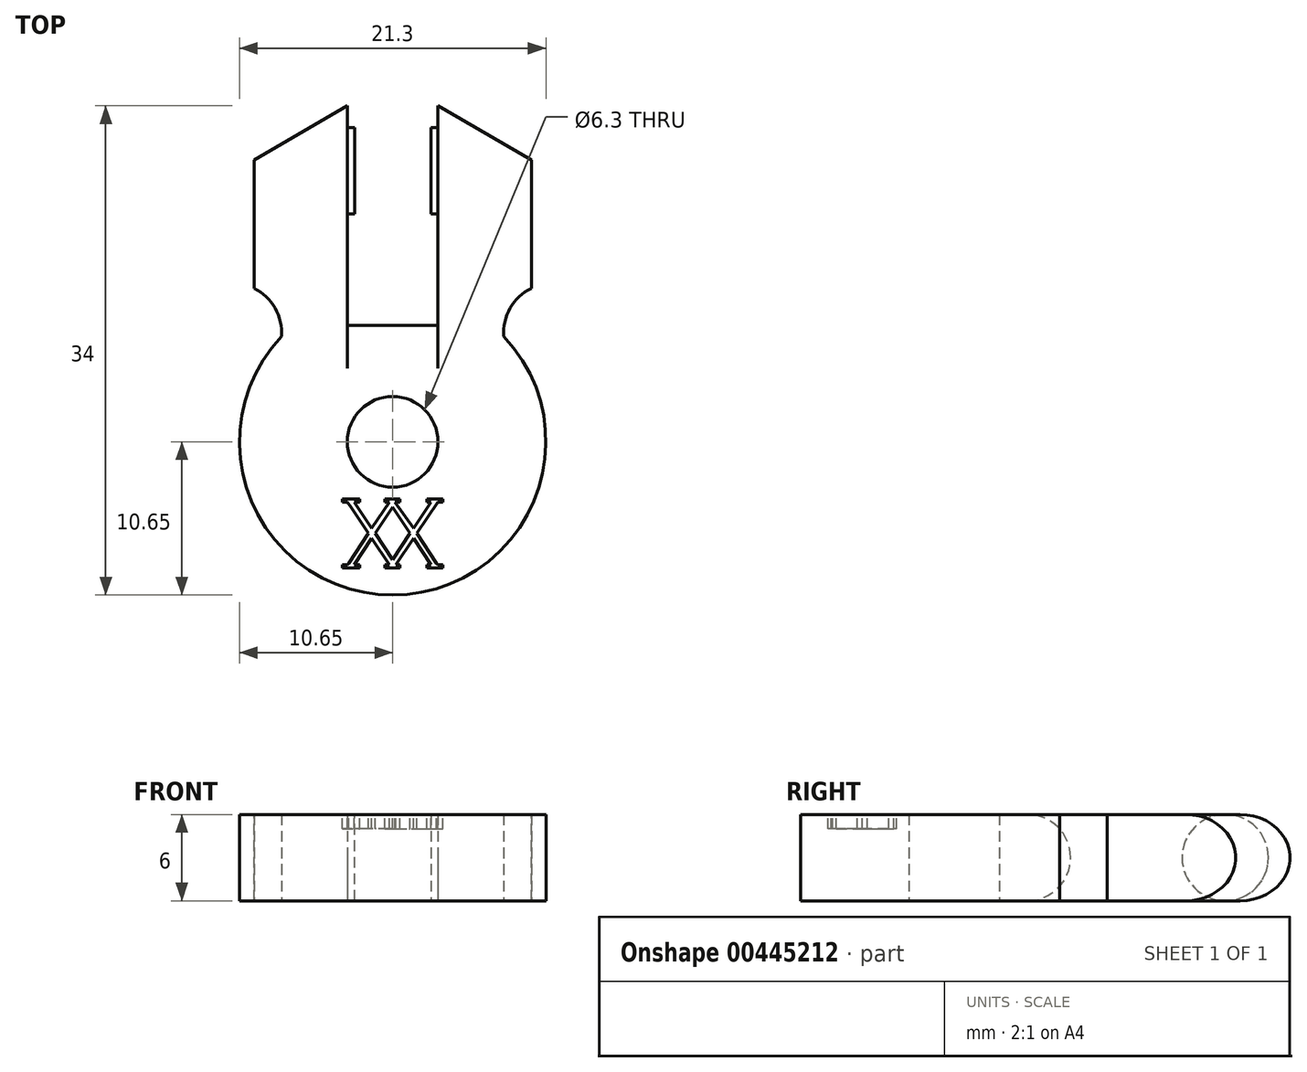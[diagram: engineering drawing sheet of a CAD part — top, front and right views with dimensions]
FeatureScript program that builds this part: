
annotation { "Feature Type Name" : "Feature", "Feature Type Description" : "" }
export const myFeature = defineFeature(function(context is Context, id is Id, definition is map)
    precondition{}
    {
        {
            var Q0;
            Q0=qCreatedBy(makeId("Top.planeOp"),FACE);
            var sketch = newSketch(context, id + "F0", { "sketchPlane" : qUnion([Q0])});
            skArc(sketch, "E0", {"start": v(-3.15, 10.17) * mm, "mid": v(0, -10.65) * mm, "end": v(3.15, 10.17) * mm});
            skCircle(sketch, "E1", {"center": v(0, 0) * mm, "radius": 3.15 * mm});
            skPoint(sketch, "E2", {"position": v(0, 8.1) * mm});
            skLineSegment(sketch, "E3", {"start": v(0, 8.1) * mm, "end": v(3.15, 8.1) * mm});
            skLineSegment(sketch, "E4", {"start": v(0, 8.1) * mm, "end": v(-3.15, 8.1) * mm});
            skLineSegment(sketch, "E5", {"start": v(0, 0) * mm, "end": v(0, 8.1) * mm});
            skLineSegment(sketch, "E6", {"start": v(-3.15, 8.1) * mm, "end": v(-3.15, 23.35) * mm});
            skLineSegment(sketch, "E7", {"start": v(-9.64, 19.59) * mm, "end": v(-9.64, 10.66) * mm});
            skLineSegment(sketch, "E8", {"start": v(-9.64, 19.59) * mm, "end": v(-3.15, 23.35) * mm});
            skArc(sketch, "E9", {"start": v(-7.72, 7.33) * mm, "mid": v(-8.17, 9.3) * mm, "end": v(-9.64, 10.66) * mm});
            skPoint(sketch, "E10.orphan", {"position": v(-9.64, 4.53) * mm});
            skLineSegment(sketch, "E11.MirrorCS", {"start": v(3.15, 8.1) * mm, "end": v(3.15, 23.35) * mm});
            skLineSegment(sketch, "E12.MirrorCS", {"start": v(9.64, 19.59) * mm, "end": v(3.15, 23.35) * mm});
            skLineSegment(sketch, "E13.MirrorCS", {"start": v(9.64, 19.59) * mm, "end": v(9.64, 10.66) * mm});
            skArc(sketch, "E14.MirrorCS", {"start": v(7.72, 7.33) * mm, "mid": v(8.17, 9.3) * mm, "end": v(9.64, 10.66) * mm});
            skSolve(sketch);
        }
        {
            var Q0;
            Q0=qSketchRegion(id+"F0",true);
            extrude(context, id + "F1", {"entities" : qUnion([Q0]), "depth" : 6 * mm});
        }
        {
            var Q0;
            Q0=makeQuery(id+"F1.opExtrude","SWEPT_FACE",FACE,{"disambiguationData":[OSD([sQuery(id+"F0.wireOp",EDGE,"E6")])]});
            var sketch = newSketch(context, id + "F2", { "sketchPlane" : qUnion([Q0])});
            skLineSegment(sketch, "E15", {"start": v(23.35, 6) * mm, "end": v(23.35, 0) * mm});
            skPoint(sketch, "E16", {"position": v(23.35, 3) * mm});
            skCircle(sketch, "E17", {"center": v(18.85, 3) * mm, "radius": 3 * mm});
            skSolve(sketch);
        }
        {
            var Q0;
            Q0=qSketchRegion(id+"F2",true);
            extrude(context, id + "F3", {"entities" : qUnion([Q0]), "operationType" : NewBodyOperationType.ADD, "depth" : 0.5 * mm});
        }
        {
            var Q0;
            Q0=makeQuery(id+"F1.opExtrude","SWEPT_FACE",FACE,{"disambiguationData":[OSD([sQuery(id+"F0.wireOp",EDGE,"E11.MirrorCS")])]});
            var sketch = newSketch(context, id + "F4", { "sketchPlane" : qUnion([Q0])});
            skPoint(sketch, "E18", {"position": v(-23.35, 3) * mm});
            skCircle(sketch, "E19", {"center": v(-18.85, 3) * mm, "radius": 3 * mm});
            skSolve(sketch);
        }
        {
            var Q0;
            Q0=qSketchRegion(id+"F4",true);
            extrude(context, id + "F5", {"entities" : qUnion([Q0]), "operationType" : NewBodyOperationType.ADD, "depth" : 0.5 * mm});
        }
        {
            var Q0;
            Q0=makeQuery(id+"F1.opExtrude","CAP_EDGE",EDGE,{"disambiguationData":[OSD([sQuery(id+"F0.wireOp",EDGE,"E8")])],"isStart":true});
            var Q1;
            Q1=makeQuery(id+"F1.opExtrude","CAP_EDGE",EDGE,{"disambiguationData":[OSD([sQuery(id+"F0.wireOp",EDGE,"E8")])],"isStart":false});
            fillet(context, id + "F6", {"entities" : qUnion([Q0, Q1]), "radius" : 3 * mm, "tangentPropagation" : true, "allowEdgeOverflow" : false});
        }
        {
            var Q0;
            Q0=makeQuery(id+"F1.opExtrude","CAP_EDGE",EDGE,{"disambiguationData":[OSD([sQuery(id+"F0.wireOp",EDGE,"E12.MirrorCS")])],"isStart":true});
            var Q1;
            Q1=makeQuery(id+"F1.opExtrude","CAP_EDGE",EDGE,{"disambiguationData":[OSD([sQuery(id+"F0.wireOp",EDGE,"E12.MirrorCS")])],"isStart":false});
            fillet(context, id + "F7", {"entities" : qUnion([Q0, Q1]), "radius" : 3 * mm, "tangentPropagation" : true, "allowEdgeOverflow" : false});
        }
        {
            var Q0;
            Q0=makeQuery(id+"F1.opExtrude","CAP_FACE",FACE,{"disambiguationData":[OSD([sQuery(id+"F0.wireOp",EDGE,"E0"),sQuery(id+"F0.wireOp",EDGE,"E1"),sQuery(id+"F0.wireOp",EDGE,"E3"),sQuery(id+"F0.wireOp",EDGE,"E4"),sQuery(id+"F0.wireOp",EDGE,"E6"),sQuery(id+"F0.wireOp",EDGE,"E7"),sQuery(id+"F0.wireOp",EDGE,"E8"),sQuery(id+"F0.wireOp",EDGE,"E9"),sQuery(id+"F0.wireOp",EDGE,"E11.MirrorCS"),sQuery(id+"F0.wireOp",EDGE,"E12.MirrorCS"),sQuery(id+"F0.wireOp",EDGE,"E13.MirrorCS"),sQuery(id+"F0.wireOp",EDGE,"E14.MirrorCS")])],"isStart":false});
            var sketch = newSketch(context, id + "F8", { "sketchPlane" : qUnion([Q0])});
            skLineSegment(sketch, "E20.0", {"start": v(-0.23, -4.2) * mm, "end": v(-1.45, -6.02) * mm});
            skLineSegment(sketch, "E21.MirrorCS", {"start": v(0, -4.54) * mm, "end": v(-1.22, -6.37) * mm});
            skLineSegment(sketch, "E22.0", {"start": v(0, -8.2) * mm, "end": v(-1.22, -6.37) * mm});
            skLineSegment(sketch, "E23.MirrorCS", {"start": v(-0.23, -8.54) * mm, "end": v(-1.45, -6.72) * mm});
            skLineSegment(sketch, "E24.trimOffspring", {"start": v(-1.45, -6.02) * mm, "end": v(-2.67, -4.2) * mm});
            skLineSegment(sketch, "E25.trimOffspring", {"start": v(-1.45, -6.72) * mm, "end": v(-2.67, -8.54) * mm});
            skLineSegment(sketch, "E26.trimOffspring", {"start": v(-1.68, -6.37) * mm, "end": v(-2.9, -4.54) * mm});
            skLineSegment(sketch, "E27.trimOffspring", {"start": v(-1.68, -6.37) * mm, "end": v(-3.06, -8.44) * mm});
            skLineSegment(sketch, "E28.MirrorCS", {"start": v(0, -4.54) * mm, "end": v(1.22, -6.37) * mm});
            skLineSegment(sketch, "E29.MirrorCS", {"start": v(1.45, -6.02) * mm, "end": v(2.67, -4.2) * mm});
            skLineSegment(sketch, "E30.MirrorCS", {"start": v(1.68, -6.37) * mm, "end": v(2.9, -4.54) * mm});
            skLineSegment(sketch, "E31.MirrorCS", {"start": v(1.68, -6.37) * mm, "end": v(3.06, -8.44) * mm});
            skLineSegment(sketch, "E32.MirrorCS", {"start": v(1.45, -6.72) * mm, "end": v(2.67, -8.54) * mm});
            skLineSegment(sketch, "E33.MirrorCS", {"start": v(0.23, -8.54) * mm, "end": v(1.45, -6.72) * mm});
            skLineSegment(sketch, "E34.MirrorCS", {"start": v(0, -8.2) * mm, "end": v(1.22, -6.37) * mm});
            skLineSegment(sketch, "E35", {"start": v(0.16, -4.2) * mm, "end": v(0.5, -4.2) * mm});
            skLineSegment(sketch, "E36", {"start": v(-0.23, -4.2) * mm, "end": v(-0.54, -4.2) * mm});
            skLineSegment(sketch, "E37", {"start": v(-2.9, -4.54) * mm, "end": v(-3.13, -4.2) * mm});
            skLineSegment(sketch, "E38", {"start": v(2.9, -4.54) * mm, "end": v(3.13, -4.2) * mm});
            skLineSegment(sketch, "E39", {"start": v(3.06, -8.44) * mm, "end": v(3.14, -8.54) * mm});
            skLineSegment(sketch, "E40", {"start": v(-3.06, -8.44) * mm, "end": v(-3.14, -8.54) * mm});
            skLineSegment(sketch, "E41", {"start": v(-3.5, -4.2) * mm, "end": v(-3.13, -4.2) * mm});
            skLineSegment(sketch, "E42", {"start": v(-0.54, -4.2) * mm, "end": v(-0.23, -4.2) * mm});
            skLineSegment(sketch, "E43", {"start": v(2.38, -4.2) * mm, "end": v(2.67, -4.2) * mm});
            skLineSegment(sketch, "E44", {"start": v(-3.5, -4.2) * mm, "end": v(-3.5, -3.98) * mm});
            skLineSegment(sketch, "E45", {"start": v(-3.5, -3.98) * mm, "end": v(-2.3, -3.98) * mm});
            skLineSegment(sketch, "E46", {"start": v(3.5, -3.98) * mm, "end": v(3.5, -4.2) * mm});
            skLineSegment(sketch, "E47", {"start": v(-2.3, -4.2) * mm, "end": v(-2.3, -3.98) * mm});
            skLineSegment(sketch, "E48", {"start": v(-0.54, -4.2) * mm, "end": v(-0.54, -3.98) * mm});
            skLineSegment(sketch, "E49", {"start": v(0.5, -4.2) * mm, "end": v(0.5, -3.98) * mm});
            skLineSegment(sketch, "E50.trimOffspring", {"start": v(-0.54, -3.98) * mm, "end": v(0.5, -3.98) * mm});
            skLineSegment(sketch, "E51.trimOffspring", {"start": v(-2.3, -4.2) * mm, "end": v(-2.67, -4.2) * mm});
            skLineSegment(sketch, "E52.trimOffspring", {"start": v(-2.67, -4.2) * mm, "end": v(-2.3, -4.2) * mm});
            skLineSegment(sketch, "E53.trimOffspring", {"start": v(-3.13, -4.2) * mm, "end": v(-3.5, -4.2) * mm});
            skLineSegment(sketch, "E54", {"start": v(2.38, -4.2) * mm, "end": v(2.38, -3.98) * mm});
            skLineSegment(sketch, "E55.trimOffspring", {"start": v(2.38, -3.98) * mm, "end": v(3.5, -3.98) * mm});
            skLineSegment(sketch, "E56.trimOffspring", {"start": v(3.13, -4.2) * mm, "end": v(3.36, -4.2) * mm});
            skLineSegment(sketch, "E57.trimOffspring", {"start": v(3.13, -4.2) * mm, "end": v(3.5, -4.2) * mm});
            skLineSegment(sketch, "E58.trimOffspring", {"start": v(3.13, -8.54) * mm, "end": v(3.14, -8.54) * mm});
            skLineSegment(sketch, "E59.MirrorCS", {"start": v(-0.54, -8.75) * mm, "end": v(0.5, -8.75) * mm});
            skLineSegment(sketch, "E60.MirrorCS", {"start": v(-0.54, -8.54) * mm, "end": v(-0.54, -8.75) * mm});
            skLineSegment(sketch, "E61.MirrorCS", {"start": v(-0.23, -8.54) * mm, "end": v(-0.54, -8.54) * mm});
            skLineSegment(sketch, "E62.MirrorCS", {"start": v(0.23, -8.54) * mm, "end": v(0.5, -8.54) * mm});
            skLineSegment(sketch, "E63.MirrorCS", {"start": v(0.5, -8.54) * mm, "end": v(0.5, -8.75) * mm});
            skLineSegment(sketch, "E64.MirrorCS", {"start": v(-3.13, -8.54) * mm, "end": v(-3.5, -8.54) * mm});
            skLineSegment(sketch, "E65.MirrorCS", {"start": v(-3.5, -8.54) * mm, "end": v(-3.5, -8.75) * mm});
            skLineSegment(sketch, "E66.MirrorCS", {"start": v(-3.5, -8.75) * mm, "end": v(-2.3, -8.75) * mm});
            skLineSegment(sketch, "E67.MirrorCS", {"start": v(-2.3, -8.54) * mm, "end": v(-2.3, -8.75) * mm});
            skLineSegment(sketch, "E68.MirrorCS", {"start": v(-2.67, -8.54) * mm, "end": v(-2.3, -8.54) * mm});
            skLineSegment(sketch, "E69.MirrorCS", {"start": v(2.38, -8.75) * mm, "end": v(3.5, -8.75) * mm});
            skLineSegment(sketch, "E70.MirrorCS", {"start": v(3.5, -8.75) * mm, "end": v(3.5, -8.54) * mm});
            skLineSegment(sketch, "E71.MirrorCS", {"start": v(3.13, -8.54) * mm, "end": v(3.5, -8.54) * mm});
            skLineSegment(sketch, "E72.MirrorCS", {"start": v(2.38, -8.54) * mm, "end": v(2.67, -8.54) * mm});
            skLineSegment(sketch, "E73.MirrorCS", {"start": v(2.38, -8.54) * mm, "end": v(2.38, -8.75) * mm});
            skLineSegment(sketch, "E74", {"start": v(0.16, -4.2) * mm, "end": v(1.45, -6.02) * mm});
            skSolve(sketch);
        }
        {
            var Q0;
            Q0=qSketchRegion(id+"F8",true);
            extrude(context, id + "F9", {"entities" : qUnion([Q0]), "operationType" : NewBodyOperationType.REMOVE, "oppositeDirection" : true, "depth" : 1 * mm});
        }
        {
            var Q0;
            Q0=makeQuery(id+"F1.opExtrude","CAP_EDGE",EDGE,{"disambiguationData":[OSD([sQuery(id+"F0.wireOp",EDGE,"E3"),sQuery(id+"F0.wireOp",EDGE,"E4")])],"isStart":false});
            fillet(context, id + "F10", {"entities" : qUnion([Q0]), "radius" : 3 * mm, "tangentPropagation" : true, "allowEdgeOverflow" : false});
        }
        {
            var Q0;
            Q0=makeQuery(id+"F1.opExtrude","CAP_EDGE",EDGE,{"disambiguationData":[OSD([sQuery(id+"F0.wireOp",EDGE,"E3"),sQuery(id+"F0.wireOp",EDGE,"E4")])],"isStart":true});
            fillet(context, id + "F11", {"entities" : qUnion([Q0]), "radius" : 3 * mm, "tangentPropagation" : true, "allowEdgeOverflow" : false});
        }
    });
